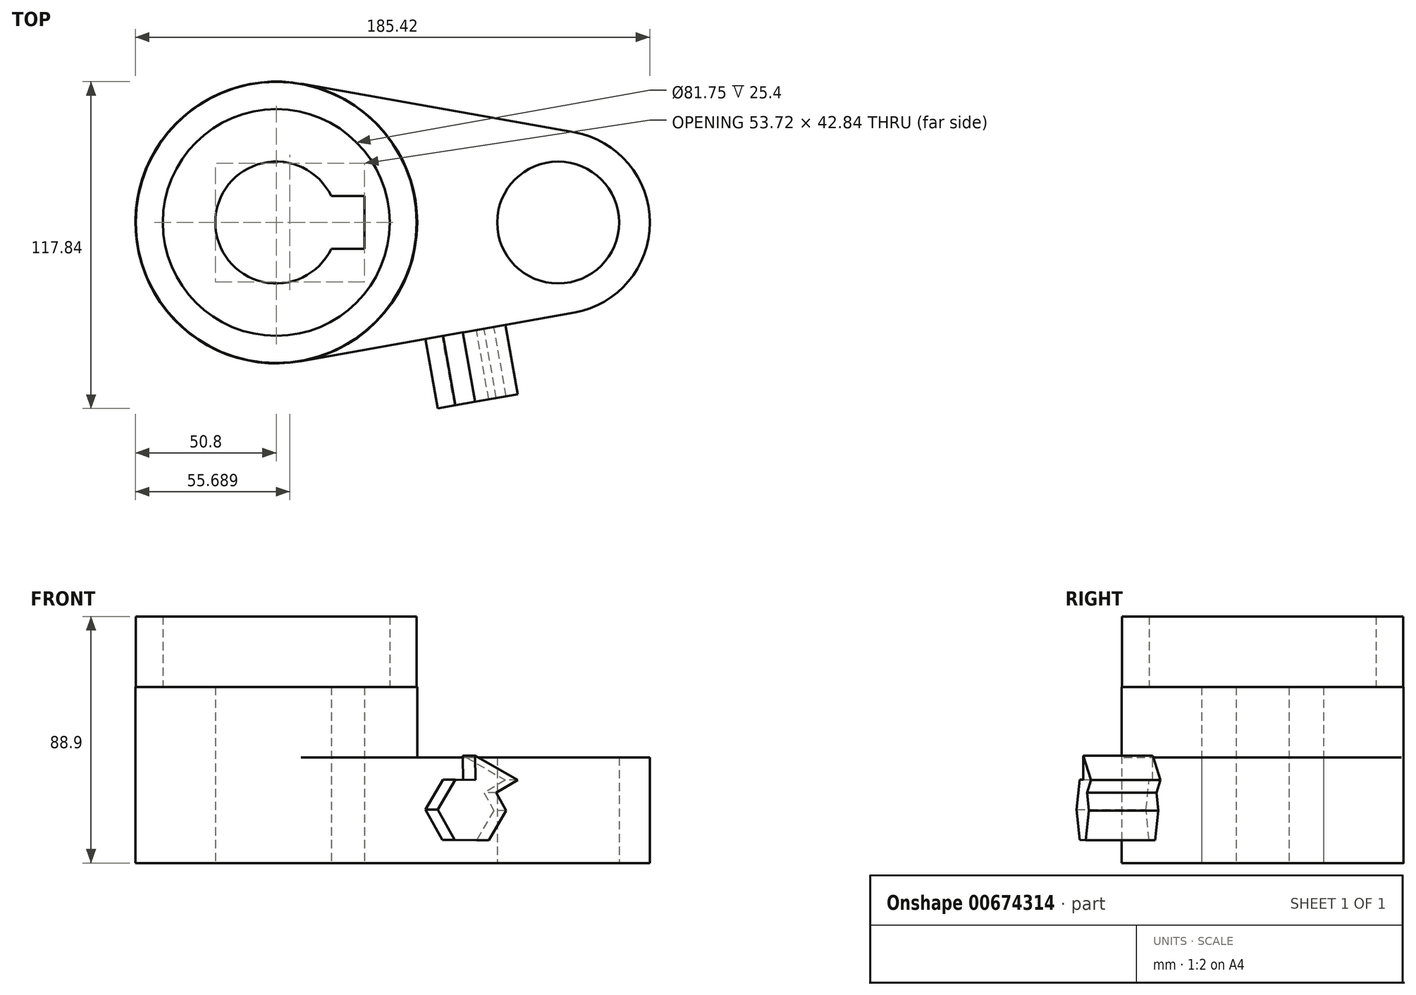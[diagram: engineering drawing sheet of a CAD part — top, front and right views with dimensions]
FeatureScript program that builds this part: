
annotation { "Feature Type Name" : "Feature", "Feature Type Description" : "" }
export const myFeature = defineFeature(function(context is Context, id is Id, definition is map)
    precondition{}
    {
        {
            var Q0;
            Q0=qCreatedBy(makeId("Top.planeOp"),FACE);
            var sketch = newSketch(context, id + "F0", { "sketchPlane" : qUnion([Q0])});
            skCircle(sketch, "E0", {"center": v(0, 0) * mm, "radius": 50.8 * mm});
            skCircle(sketch, "E1", {"center": v(101.6, 0) * mm, "radius": 33.02 * mm});
            skLineSegment(sketch, "E2", {"start": v(8.89, 50.02) * mm, "end": v(107.38, 32.51) * mm});
            skLineSegment(sketch, "E3", {"start": v(8.89, -50.02) * mm, "end": v(107.38, -32.51) * mm});
            skCircle(sketch, "E4", {"center": v(0, 0) * mm, "radius": 21.97 * mm});
            skCircle(sketch, "E5", {"center": v(101.6, 0) * mm, "radius": 21.97 * mm});
            skLineSegment(sketch, "E6.bottom", {"start": v(-31.75, -9.53) * mm, "end": v(31.75, -9.53) * mm});
            skLineSegment(sketch, "E6.top", {"start": v(-31.75, 9.53) * mm, "end": v(31.75, 9.53) * mm});
            skLineSegment(sketch, "E6.left", {"start": v(-31.75, -9.53) * mm, "end": v(-31.75, 9.53) * mm});
            skLineSegment(sketch, "E6.right", {"start": v(31.75, -9.53) * mm, "end": v(31.75, 9.53) * mm});
            skSolve(sketch);
        }
        {
            var Q0;
            Q0 = qSketchRegion(id + "F0", true);
            var Q1;
            {var subQ5=sQuery(id+"F0.wireOp",EDGE,"E6.left");Q1=makeQuery(id+"F0.imprint","IMPRINT",FACE,{"disambiguationData":[TD([[makeQuery(id+"F0.imprint","IMPRINT",EDGE,{"derivedFrom":subQ5}),-1.0]])]});}
            extrude(context, id + "F1", {"entities" : qUnion([Q0, Q1]), "depth" : 38.1 * mm, "offsetDistance" : 25.4 * mm});
        }
        {
            var Q0;
            {var subQ7=sQuery(id+"F0.wireOp",EDGE,"E6.left");Q0=makeQuery(id+"F0.imprint","IMPRINT",FACE,{"disambiguationData":[TD([[makeQuery(id+"F0.imprint","IMPRINT",EDGE,{"derivedFrom":subQ7}),1.0]])]});}
            var Q1;
            {var subQ5=sQuery(id+"F0.wireOp",EDGE,"E6.left");Q1=makeQuery(id+"F0.imprint","IMPRINT",FACE,{"disambiguationData":[TD([[makeQuery(id+"F0.imprint","IMPRINT",EDGE,{"derivedFrom":subQ5}),-1.0]])]});}
            extrude(context, id + "F2", {"entities" : qUnion([Q0, Q1]), "operationType" : NewBodyOperationType.ADD, "depth" : 63.5 * mm, "offsetDistance" : 25.4 * mm});
        }
        {
            var Q0;
            Q0=makeQuery(id+"F1.opExtrude","SWEPT_FACE",FACE,{"disambiguationData":[OSD([sQuery(id+"F0.wireOp",EDGE,"E3")])]});
            var sketch = newSketch(context, id + "F3", { "sketchPlane" : qUnion([Q0])});
            skLineSegment(sketch, "E7.bottom", {"start": v(77.46, 14.86) * mm, "end": v(39.36, 14.86) * mm});
            skLineSegment(sketch, "E7.top", {"start": v(77.46, 25.02) * mm, "end": v(39.36, 25.02) * mm});
            skLineSegment(sketch, "E7.left", {"start": v(77.46, 14.86) * mm, "end": v(77.46, 25.02) * mm});
            skLineSegment(sketch, "E7.right", {"start": v(39.36, 14.86) * mm, "end": v(39.36, 25.02) * mm});
            skPoint(sketch, "E7.middle", {"position": v(58.41, 19.94) * mm});
            skSolve(sketch);
        }
        {
            var Q0;
            Q0=makeQuery(id+"F3.imprint","IMPRINT",FACE,{"disambiguationData":[TD([[makeQuery(id+"F3.imprint","IMPRINT",EDGE,{"derivedFrom":sQuery(id+"F3.wireOp",EDGE,"E7.bottom")}),1.0]])]});
            var sketch = newSketch(context, id + "F4", { "sketchPlane" : qUnion([Q0])});
            skCircle(sketch, "E8.cCircle", {"center": v(58.13, 19.08) * mm, "radius": 12.51 * mm, "construction": true});
            skLineSegment(sketch, "E8.0", {"start": v(70.64, 18.92) * mm, "end": v(64.24, 8.16) * mm});
            skLineSegment(sketch, "E8.1", {"start": v(64.24, 8.16) * mm, "end": v(51.73, 8.33) * mm});
            skLineSegment(sketch, "E8.2", {"start": v(51.73, 8.33) * mm, "end": v(45.61, 19.25) * mm});
            skLineSegment(sketch, "E8.3", {"start": v(45.61, 19.25) * mm, "end": v(52.01, 30) * mm});
            skLineSegment(sketch, "E8.4", {"start": v(52.01, 30) * mm, "end": v(64.53, 29.84) * mm});
            skLineSegment(sketch, "E8.5", {"start": v(64.53, 29.84) * mm, "end": v(70.64, 18.92) * mm});
            skCircle(sketch, "E9.cCircle", {"center": v(64.53, 29.84) * mm, "radius": 10.33 * mm, "construction": true});
            skPoint(sketch, "E9.cCircle.perimeterSnap0", {"position": v(58.27, 29.92) * mm});
            skLineSegment(sketch, "E9.0", {"start": v(74.85, 29.92) * mm, "end": v(59.43, 20.85) * mm});
            skPoint(sketch, "E9.0.startSnap0", {"position": v(58.27, 29.92) * mm});
            skLineSegment(sketch, "E9.1", {"start": v(59.43, 20.85) * mm, "end": v(59.3, 38.74) * mm});
            skLineSegment(sketch, "E9.2", {"start": v(59.3, 38.74) * mm, "end": v(74.85, 29.92) * mm});
            skSolve(sketch);
        }
        {
            var Q0;
            Q0 = qSketchRegion(id + "F4", true);
            extrude(context, id + "F5", {"entities" : qUnion([Q0]), "operationType" : NewBodyOperationType.ADD, "depth" : 25.4 * mm, "offsetDistance" : 25.4 * mm});
        }
        {
            var Q0;
            Q0=makeQuery(id+"F2.opExtrude","CAP_FACE",FACE,{"disambiguationData":[OSD([sQuery(id+"F0.wireOp",EDGE,"E0"),sQuery(id+"F0.wireOp",EDGE,"E4"),sQuery(id+"F0.wireOp",EDGE,"E6.bottom"),sQuery(id+"F0.wireOp",EDGE,"E6.top"),sQuery(id+"F0.wireOp",EDGE,"E6.right")])],"isStart":false});
            var sketch = newSketch(context, id + "F6", { "sketchPlane" : qUnion([Q0])});
            skCircle(sketch, "E10", {"center": v(0, 0) * mm, "radius": 40.87 * mm});
            skCircle(sketch, "E11", {"center": v(0, 0) * mm, "radius": 50.65 * mm});
            skSolve(sketch);
        }
        {
            var Q0;
            Q0 = qSketchRegion(id + "F6", true);
            extrude(context, id + "F7", {"entities" : qUnion([Q0]), "operationType" : NewBodyOperationType.ADD, "depth" : 25.4 * mm, "offsetDistance" : 25.4 * mm});
        }
    });
